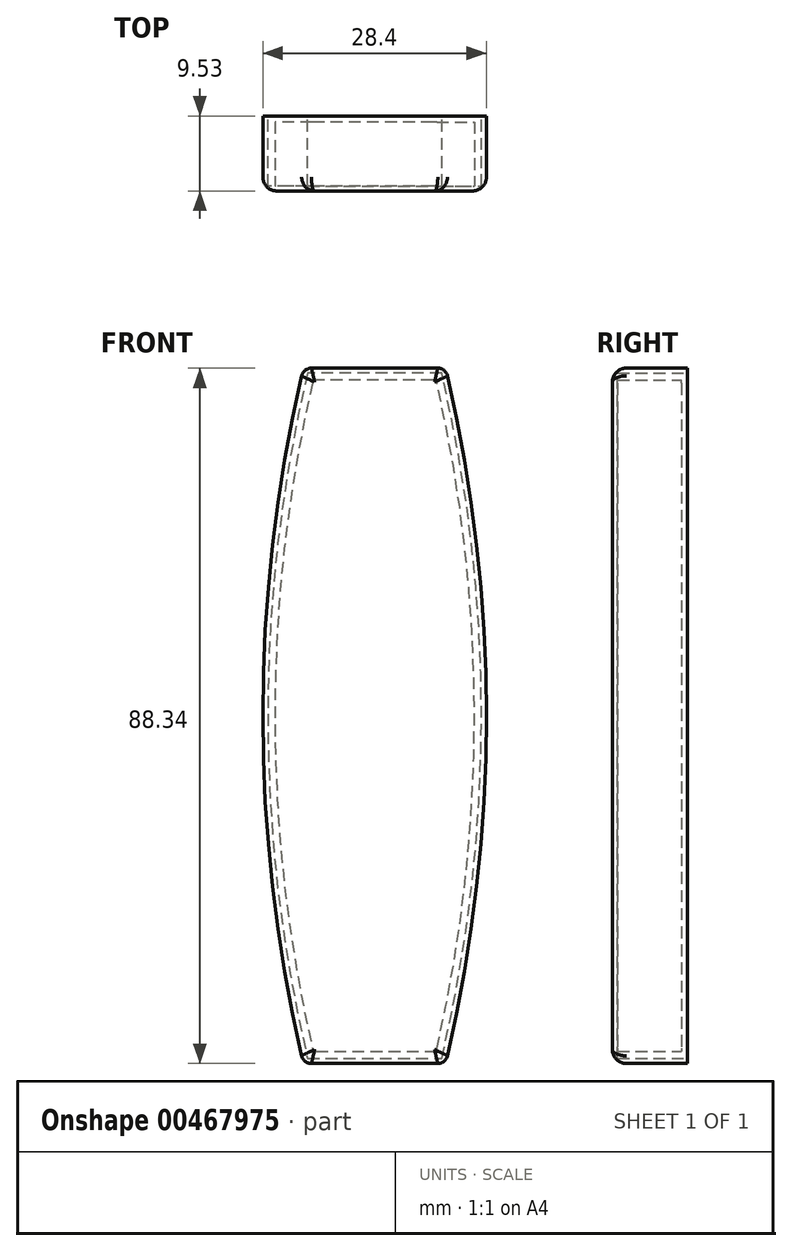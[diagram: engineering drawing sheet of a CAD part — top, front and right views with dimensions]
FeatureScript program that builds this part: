
annotation { "Feature Type Name" : "Feature", "Feature Type Description" : "" }
export const myFeature = defineFeature(function(context is Context, id is Id, definition is map)
    precondition{}
    {
        {
            var Q0;
            Q0=qCreatedBy(makeId("Front.planeOp"),FACE);
            var sketch = newSketch(context, id + "F0", { "sketchPlane" : qUnion([Q0])});
            skLineSegment(sketch, "E0", {"start": v(8.5, 15) * mm, "end": v(8.5, -15) * mm});
            skArc(sketch, "E1", {"start": v(-8.5, -15) * mm, "mid": v(0, -23.5) * mm, "end": v(8.5, -15) * mm});
            skLineSegment(sketch, "E2", {"start": v(-8.5, -15) * mm, "end": v(-8.5, 15) * mm});
            skArc(sketch, "E3", {"start": v(8.5, 15) * mm, "mid": v(0, 23.5) * mm, "end": v(-8.5, 15) * mm});
            skLineSegment(sketch, "E4.0", {"start": v(9.03, 44.17) * mm, "end": v(-9.03, 44.17) * mm});
            skArc(sketch, "E4.1", {"start": v(9.03, -44.17) * mm, "mid": v(14.2, 0) * mm, "end": v(9.03, 44.17) * mm});
            skLineSegment(sketch, "E4.2", {"start": v(-9.03, -44.17) * mm, "end": v(9.03, -44.17) * mm});
            skArc(sketch, "E4.3", {"start": v(-9.03, 44.17) * mm, "mid": v(-14.2, 0) * mm, "end": v(-9.03, -44.17) * mm});
            skSolve(sketch);
        }
        {
            var Q0;
            Q0=makeQuery(id+"F0.imprint","IMPRINT",FACE,{"disambiguationData":[TD([[makeQuery(id+"F0.imprint","IMPRINT",EDGE,{"derivedFrom":sQuery(id+"F0.wireOp",EDGE,"E0")}),1.0]])]});
            var Q1;
            Q1=makeQuery(id+"F0.imprint","IMPRINT",FACE,{"disambiguationData":[TD([[makeQuery(id+"F0.imprint","IMPRINT",EDGE,{"derivedFrom":sQuery(id+"F0.wireOp",EDGE,"E0")}),-1.0]])]});
            extrude(context, id + "F1", {"entities" : qUnion([Q0, Q1]), "depth" : 9.52 * mm, "offsetDistance" : 25.4 * mm});
        }
        {
            var Q0;
            Q0=makeQuery(id+"F1.opExtrude","CAP_FACE",FACE,{"disambiguationData":[OSD([sQuery(id+"F0.wireOp",EDGE,"E4.0"),sQuery(id+"F0.wireOp",EDGE,"E4.1"),sQuery(id+"F0.wireOp",EDGE,"E4.2"),sQuery(id+"F0.wireOp",EDGE,"E4.3")])],"isStart":true});
            shell(context, id + "F2", {"entities" : qUnion([Q0]), "thickness" : 0.64 * mm});
        }
        {
            var Q0;
            Q0=makeQuery(id+"F1.opExtrude","CAP_EDGE",EDGE,{"disambiguationData":[OSD([sQuery(id+"F0.wireOp",EDGE,"E4.3")])],"isStart":false});
            var Q1;
            Q1=makeQuery(id+"F1.opExtrude","CAP_EDGE",EDGE,{"disambiguationData":[OSD([sQuery(id+"F0.wireOp",EDGE,"E4.0")])],"isStart":false});
            var Q2;
            Q2=makeQuery(id+"F1.opExtrude","CAP_EDGE",EDGE,{"disambiguationData":[OSD([sQuery(id+"F0.wireOp",EDGE,"E4.1")])],"isStart":false});
            var Q3;
            Q3=makeQuery(id+"F1.opExtrude","CAP_EDGE",EDGE,{"disambiguationData":[OSD([sQuery(id+"F0.wireOp",EDGE,"E4.2")])],"isStart":false});
            fillet(context, id + "F3", {"entities" : qUnion([Q0, Q1, Q2, Q3]), "radius" : 1.78 * mm, "tangentPropagation" : true, "allowEdgeOverflow" : false});
        }
        {
            var Q0;
            Q0=makeQuery(id+"F2.opShell","OFFSET_FACE",FACE,{"disambiguationData":[OSD([sQuery(id+"F0.wireOp",EDGE,"E4.0"),sQuery(id+"F0.wireOp",EDGE,"E4.1"),sQuery(id+"F0.wireOp",EDGE,"E4.2"),sQuery(id+"F0.wireOp",EDGE,"E4.3")])]});
            var sketch = newSketch(context, id + "F4", { "sketchPlane" : qUnion([Q0])});
            skArc(sketch, "E5.0", {"start": v(-7.82, -42.65) * mm, "mid": v(-12.68, 0) * mm, "end": v(-7.82, 42.65) * mm});
            skLineSegment(sketch, "E5.1", {"start": v(7.82, -42.65) * mm, "end": v(-7.82, -42.65) * mm});
            skArc(sketch, "E5.2", {"start": v(7.82, 42.65) * mm, "mid": v(12.68, 0) * mm, "end": v(7.82, -42.65) * mm});
            skLineSegment(sketch, "E5.3", {"start": v(-7.82, 42.65) * mm, "end": v(7.82, 42.65) * mm});
            skSolve(sketch);
        }
        {
            var Q0;
            Q0=makeQuery(id+"F1.opExtrude","SWEPT_EDGE",EDGE,{"disambiguationData":[OSD([sQuery(id+"F0.wireOp",EDGE,"E4.1"),sQuery(id+"F0.wireOp",EDGE,"E4.2")])]});
            var Q1;
            Q1=makeQuery(id+"F1.opExtrude","SWEPT_EDGE",EDGE,{"disambiguationData":[OSD([sQuery(id+"F0.wireOp",EDGE,"E4.2"),sQuery(id+"F0.wireOp",EDGE,"E4.3")])]});
            var Q2;
            Q2=makeQuery(id+"F1.opExtrude","SWEPT_EDGE",EDGE,{"disambiguationData":[OSD([sQuery(id+"F0.wireOp",EDGE,"E4.0"),sQuery(id+"F0.wireOp",EDGE,"E4.3")])]});
            var Q3;
            Q3=makeQuery(id+"F1.opExtrude","SWEPT_EDGE",EDGE,{"disambiguationData":[OSD([sQuery(id+"F0.wireOp",EDGE,"E4.0"),sQuery(id+"F0.wireOp",EDGE,"E4.1")])]});
            fillet(context, id + "F5", {"entities" : qUnion([Q0, Q1, Q2, Q3]), "radius" : 1.27 * mm, "tangentPropagation" : true, "allowEdgeOverflow" : false});
        }
        {
            var Q0;
            Q0=makeQuery(id+"F4.imprint","IMPRINT",FACE,{"disambiguationData":[TD([[makeQuery(id+"F4.imprint","IMPRINT",EDGE,{"derivedFrom":sQuery(id+"F4.wireOp",EDGE,"E5.0")}),1.0]])]});
            extrude(context, id + "F6", {"entities" : qUnion([Q0]), "operationType" : NewBodyOperationType.ADD, "depth" : 8.13 * mm, "offsetDistance" : 25.4 * mm});
        }
        {
            var Q0;
            Q0=makeQuery(id+"F6.opExtrude","SWEPT_EDGE",EDGE,{"disambiguationData":[OSD([sQuery(id+"F4.wireOp",EDGE,"E5.2"),sQuery(id+"F4.wireOp",EDGE,"E5.3")])]});
            var Q1;
            Q1=makeQuery(id+"F6.opExtrude","CAP_EDGE",EDGE,{"disambiguationData":[OSD([sQuery(id+"F4.wireOp",EDGE,"E5.3")])],"isStart":true});
            var Q2;
            Q2=makeQuery(id+"F6.opExtrude","CAP_EDGE",EDGE,{"disambiguationData":[OSD([sQuery(id+"F4.wireOp",EDGE,"E5.2")])],"isStart":true});
            var Q3;
            Q3=makeQuery(id+"F6.opExtrude","SWEPT_EDGE",EDGE,{"disambiguationData":[OSD([sQuery(id+"F4.wireOp",EDGE,"E5.0"),sQuery(id+"F4.wireOp",EDGE,"E5.3")])]});
            var Q4;
            Q4=makeQuery(id+"F6.opExtrude","CAP_EDGE",EDGE,{"disambiguationData":[OSD([sQuery(id+"F4.wireOp",EDGE,"E5.0")])],"isStart":true});
            var Q5;
            Q5=makeQuery(id+"F6.opExtrude","SWEPT_EDGE",EDGE,{"disambiguationData":[OSD([sQuery(id+"F4.wireOp",EDGE,"E5.1"),sQuery(id+"F4.wireOp",EDGE,"E5.2")])]});
            var Q6;
            Q6=makeQuery(id+"F6.opExtrude","CAP_EDGE",EDGE,{"disambiguationData":[OSD([sQuery(id+"F4.wireOp",EDGE,"E5.1")])],"isStart":true});
            var Q7;
            Q7=makeQuery(id+"F6.opExtrude","SWEPT_EDGE",EDGE,{"disambiguationData":[OSD([sQuery(id+"F4.wireOp",EDGE,"E5.0"),sQuery(id+"F4.wireOp",EDGE,"E5.1")])]});
            fillet(context, id + "F7", {"entities" : qUnion([Q0, Q1, Q2, Q3, Q4, Q5, Q6, Q7]), "radius" : 0.5 * mm, "tangentPropagation" : true, "allowEdgeOverflow" : false});
        }
    });
